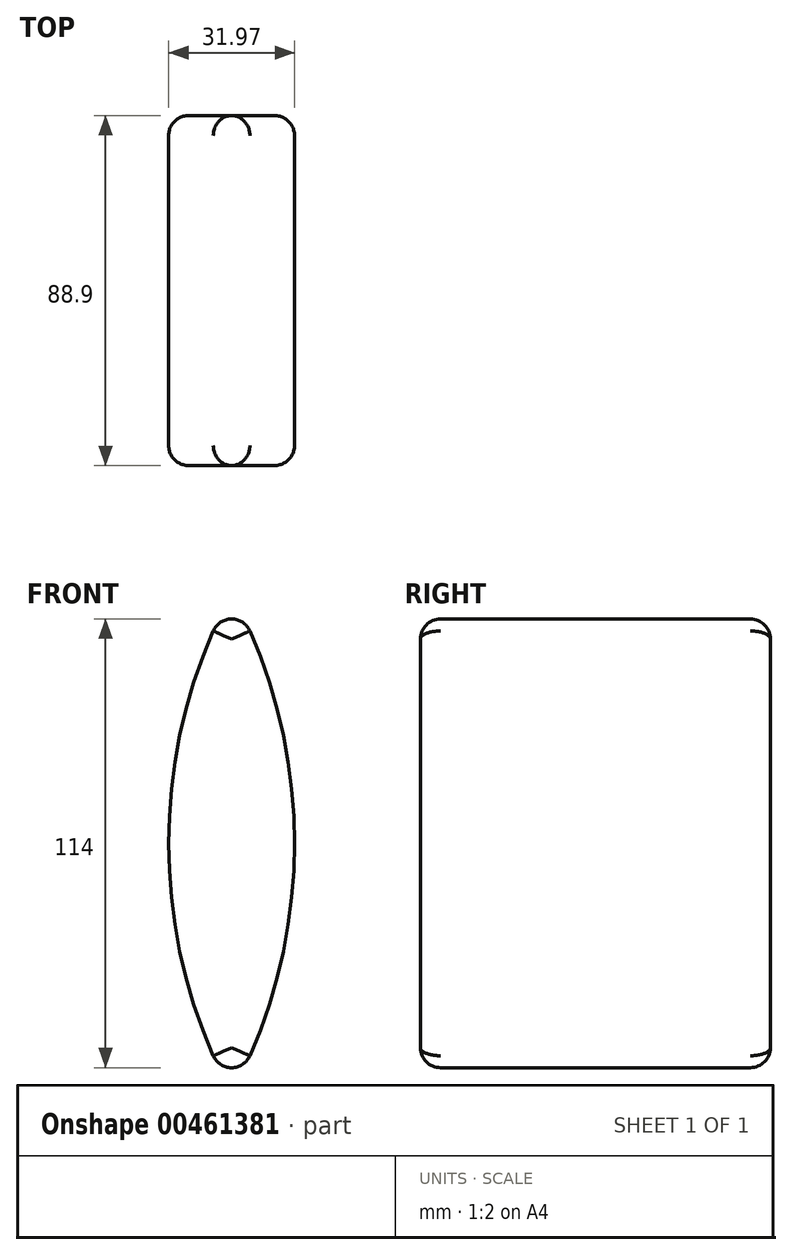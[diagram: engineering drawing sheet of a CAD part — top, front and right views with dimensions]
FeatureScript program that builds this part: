
annotation { "Feature Type Name" : "Feature", "Feature Type Description" : "" }
export const myFeature = defineFeature(function(context is Context, id is Id, definition is map)
    precondition{}
    {
        {
            var Q0;
            Q0=qCreatedBy(makeId("Front.planeOp"),FACE);
            var sketch = newSketch(context, id + "F0", { "sketchPlane" : qUnion([Q0]), "disableImprinting" : false});
            skArc(sketch, "E0", {"start": v(0, -63.73) * mm, "mid": v(15.98, -0.23) * mm, "end": v(0, 63.27) * mm});
            skArc(sketch, "E1", {"start": v(0, 63.27) * mm, "mid": v(-16, -0.23) * mm, "end": v(0, -63.73) * mm});
            skSolve(sketch);
        }
        {
            var Q0;
            Q0 = qSketchRegion(id + "F0", true);
            var Q1;
            Q1=makeQuery(id+"F0.imprint","IMPRINT",FACE,{"disambiguationData":[TD([[makeQuery(id+"F0.imprint","IMPRINT",EDGE,{"derivedFrom":sQuery(id+"F0.wireOp",EDGE,"E0")}),1.0]])]});
            extrude(context, id + "F1", {"entities" : qUnion([Q0, Q1]), "depth" : 88.9 * mm});
        }
        {
            var Q0;
            Q0=makeQuery(id+"F1.opExtrude","CAP_FACE",FACE,{"disambiguationData":[OSD([sQuery(id+"F0.wireOp",EDGE,"E0"),sQuery(id+"F0.wireOp",EDGE,"E1")])],"isStart":false});
            var Q1;
            Q1=makeQuery(id+"F1.opExtrude","CAP_FACE",FACE,{"disambiguationData":[OSD([sQuery(id+"F0.wireOp",EDGE,"E0"),sQuery(id+"F0.wireOp",EDGE,"E1")])],"isStart":true});
            fillet(context, id + "F2", {"entities" : qUnion([Q0, Q1]), "radius" : 5.08 * mm, "tangentPropagation" : true, "allowEdgeOverflow" : false});
        }
        {
            var Q0;
            {var subQ0=sQuery(id+"F0.wireOp",EDGE,"E1");var subQ1=sQuery(id+"F0.wireOp",EDGE,"E0");Q0=makeQuery(id+"F1.opExtrude","SWEPT_EDGE",EDGE,{"disambiguationData":[OSD([subQ1,subQ0]),TDD([makeQuery(id+"F0.imprint","INTERSECT",VERTEX,{"disambiguationData":[OD(1.0)],"derivedFrom":[subQ1,subQ0]})])]});}
            fillet(context, id + "F3", {"entities" : qUnion([Q0]), "radius" : 5.08 * mm, "tangentPropagation" : true, "allowEdgeOverflow" : false});
        }
        {
            var Q0;
            {var subQ0=sQuery(id+"F0.wireOp",EDGE,"E1");var subQ1=sQuery(id+"F0.wireOp",EDGE,"E0");Q0=makeQuery(id+"F1.opExtrude","SWEPT_EDGE",EDGE,{"disambiguationData":[OSD([subQ1,subQ0]),TDD([makeQuery(id+"F0.imprint","INTERSECT",VERTEX,{"disambiguationData":[OD(0.0)],"derivedFrom":[subQ1,subQ0]})])]});}
            fillet(context, id + "F4", {"entities" : qUnion([Q0]), "radius" : 5.08 * mm, "tangentPropagation" : true, "allowEdgeOverflow" : false});
        }
    });
